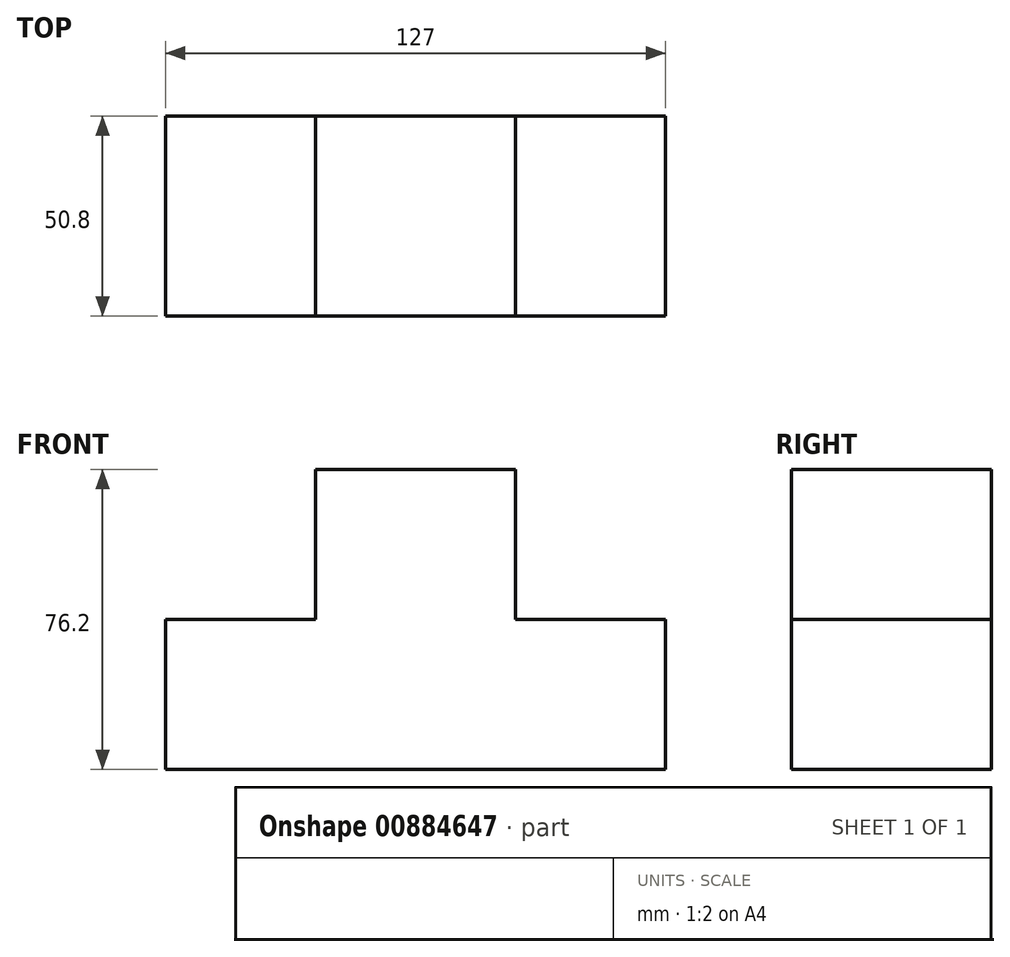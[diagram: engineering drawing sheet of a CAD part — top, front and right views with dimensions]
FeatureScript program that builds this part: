
annotation { "Feature Type Name" : "Feature", "Feature Type Description" : "" }
export const myFeature = defineFeature(function(context is Context, id is Id, definition is map)
    precondition{}
    {
        {
            var Q0;
            Q0=qCreatedBy(makeId("Top.planeOp"),FACE);
            var sketch = newSketch(context, id + "F0", { "sketchPlane" : qUnion([Q0])});
            skLineSegment(sketch, "E0.bottom", {"start": v(63.5, -25.4) * mm, "end": v(-63.5, -25.4) * mm});
            skLineSegment(sketch, "E0.top", {"start": v(63.5, 25.4) * mm, "end": v(-63.5, 25.4) * mm});
            skLineSegment(sketch, "E0.left", {"start": v(63.5, -25.4) * mm, "end": v(63.5, 25.4) * mm});
            skLineSegment(sketch, "E0.right", {"start": v(-63.5, -25.4) * mm, "end": v(-63.5, 25.4) * mm});
            skPoint(sketch, "E0.middle", {"position": v(0, 0) * mm});
            skSolve(sketch);
        }
        {
            var Q0;
            Q0 = qSketchRegion(id + "F0", true);
            extrude(context, id + "F1", {"entities" : qUnion([Q0]), "endBound" : BoundingType.SYMMETRIC, "depth" : 76.2 * mm, "offsetDistance" : 25.4 * mm});
        }
        {
            var Q0;
            Q0=makeQuery(id+"F1.opExtrude","CAP_FACE",FACE,{"disambiguationData":[OSD([sQuery(id+"F0.wireOp",EDGE,"E0.bottom"),sQuery(id+"F0.wireOp",EDGE,"E0.top"),sQuery(id+"F0.wireOp",EDGE,"E0.left"),sQuery(id+"F0.wireOp",EDGE,"E0.right")])],"isStart":false});
            var sketch = newSketch(context, id + "F2", { "sketchPlane" : qUnion([Q0])});
            skLineSegment(sketch, "E1.bottom", {"start": v(-63.5, 25.4) * mm, "end": v(-25.4, 25.4) * mm});
            skLineSegment(sketch, "E1.top", {"start": v(-63.5, -25.4) * mm, "end": v(-25.4, -25.4) * mm});
            skLineSegment(sketch, "E1.left", {"start": v(-63.5, 25.4) * mm, "end": v(-63.5, -25.4) * mm});
            skLineSegment(sketch, "E1.right", {"start": v(-25.4, 25.4) * mm, "end": v(-25.4, -25.4) * mm});
            skLineSegment(sketch, "E2.bottom", {"start": v(63.5, 25.4) * mm, "end": v(25.4, 25.4) * mm});
            skLineSegment(sketch, "E2.top", {"start": v(63.5, -25.4) * mm, "end": v(25.4, -25.4) * mm});
            skLineSegment(sketch, "E2.left", {"start": v(63.5, 25.4) * mm, "end": v(63.5, -25.4) * mm});
            skLineSegment(sketch, "E2.right", {"start": v(25.4, 25.4) * mm, "end": v(25.4, -25.4) * mm});
            skSolve(sketch);
        }
        {
            var Q0;
            Q0 = qSketchRegion(id + "F2", true);
            extrude(context, id + "F3", {"entities" : qUnion([Q0]), "operationType" : NewBodyOperationType.REMOVE, "oppositeDirection" : true, "depth" : 25.4 * mm, "offsetDistance" : 25.4 * mm});
        }
        {
            var Q0;
            Q0 = qSketchRegion(id + "F2", true);
            extrude(context, id + "F4", {"entities" : qUnion([Q0]), "operationType" : NewBodyOperationType.REMOVE, "oppositeDirection" : true, "depth" : 38.1 * mm, "offsetDistance" : 25.4 * mm});
        }
    });
